# Revit family: 353cea0d_a456_4f8f_be7a_12a71919d4d4
name_source: partatom
category: Generic Models
revit_build: Autodesk Revit Architecture 2015 (Build: 20140606_1530(x64)
units: mm (PartAtom-declared; Revit-internal decimal feet)

## types (1)
- Default
    BIMobject category = Basins
    BOSUseNativeGeometries = 1
    Date of publishing = 7/20/2017
    Design country = Italy
    EAN code = https://8030963048360
    Edition number = 1
    IFC Classification = Sanitary Terminal
    Installation instructions = http://www.ceramicaglobo.com
    Manufacturer country = Italy
    Manufacturer name = Ceramica Globo
    Masterformat 2014 Code = 22 41 16.16
    Masterformat 2014 Description = Residential Sinks
    Material main = Vitreous china
    Material secondary = Vitreous china
    NBS Reference Code = 31-75
    NBS Reference Description = Sanitary Accessories
    Nominal height = 160
    Nominal width = 600
    OmniClass Code = 23-31 13 00
    OmniClass Description = Sinks
    Product Guid = a56945c9-a590-4df1-8cd5-a5dba8084fe2
    Product SKU = Forty3-sit-on-basin-FO061
    Product data url = https://bimobject.com
    Product family = Basins
    Product group = Forty3
    Product name = Forty3 sit-on basin FO061
    Product url = http://www.ceramicaglobo.com
    QR code = http://bimobject.com
    Technical description = http://www.ceramicaglobo.com
    UNSPSC Code = 301815
    Uniclass 2.0 Code = PR-31-75
    Uniclass 2.0 Description = Sanitary Accessories
    Uniclass 2015 Code = Pr_40_20_96_15
    Uniclass 2015 Name = Ceramic sinks
    Weight Net (Kg) = 15

## geometry (parser evidence)
native form markers: Sweep x3
no freeform markers — native parametric forms only
